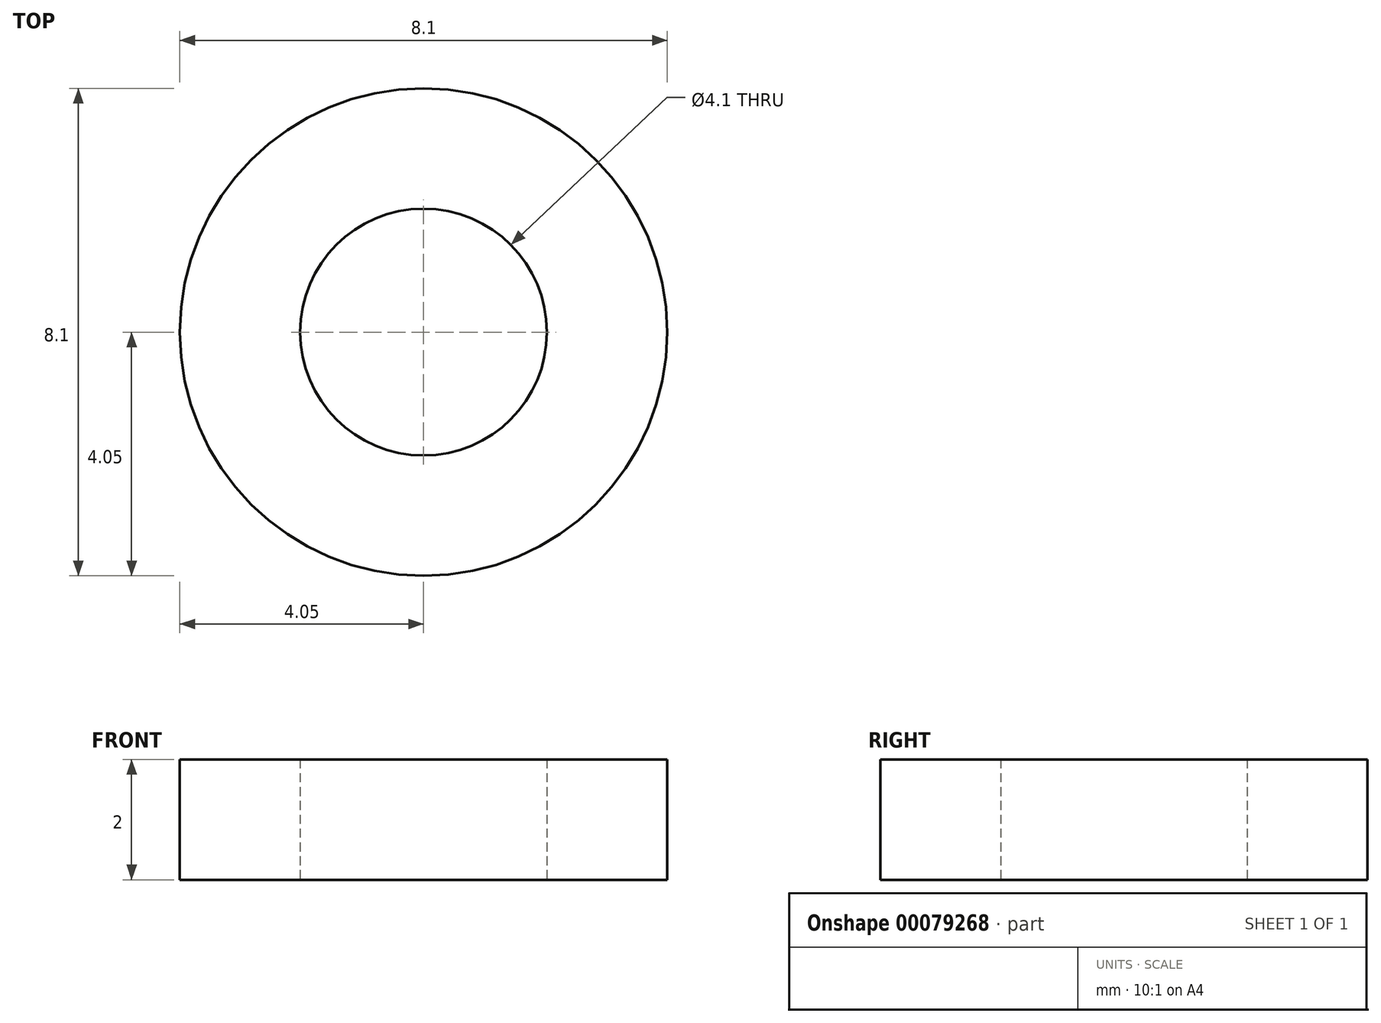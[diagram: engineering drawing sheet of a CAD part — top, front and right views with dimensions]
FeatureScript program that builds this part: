
annotation { "Feature Type Name" : "Feature", "Feature Type Description" : "" }
export const myFeature = defineFeature(function(context is Context, id is Id, definition is map)
    precondition{}
    {
        {
            var Q0;
            Q0=qCreatedBy(makeId("Top.planeOp"),FACE);
            var sketch = newSketch(context, id + "F0", { "sketchPlane" : qUnion([Q0])});
            skCircle(sketch, "E0", {"center": v(0, 0) * mm, "radius": 2.05 * mm});
            skCircle(sketch, "E1", {"center": v(0, 0) * mm, "radius": 4.05 * mm});
            skSolve(sketch);
        }
        {
            var Q0;
            Q0 = qSketchRegion(id + "F0", true);
            extrude(context, id + "F1", {"entities" : qUnion([Q0]), "depth" : 2 * mm});
        }
    });
